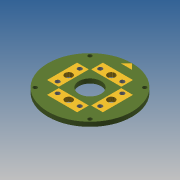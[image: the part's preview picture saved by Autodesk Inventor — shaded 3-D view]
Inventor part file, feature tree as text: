
AUTODESK INVENTOR PART (.ipt)
format: ipt  version: 2014 SP1 (Build 180222100, 222)  size: 210,944 bytes
history: native  units: in
note: dims shown in document units (in); Inventor stores cm internally (conversion verified against a paired STEP export)
features: sketch x11, hole x4, other x4, extrude x3, pattern_circular x3
ambient origin geometry x8: Origin, YZ Plane, XZ Plane, XY Plane, X Axis, Y Axis, Z Axis, Center Point
bodies: Solid1 (feature_tree)
feature tree (25):
  extrude  "Extrusion1"  Depth=0.1in TaperAngle=0.0deg
  extrude  "Extrusion2"  Depth=0.265in
  pattern_circular  "Circular Pattern1"  Count=4 Angle=360.0deg
  hole  "Hole1"  [1 undecoded]
  pattern_circular  "Circular Pattern2"  Count=4 Angle=360.0deg
  hole  "Hole2"  [1 undecoded]
  hole  "Hole3"  [1 undecoded]
  pattern_circular  "Circular Pattern3"  [2 undecoded]
  extrude  "Extrusion3"  TaperAngle=45.0deg  [1 undecoded]
  hole  "Hole4"  [1 undecoded]
  sketch  "Sketch8"  dims[d35=0.115in]
  other  "Pol1_1"
  sketch  "Sketch9"  dims[d36=0.169in d37=0.75in d38=0.375in d39=0.25in d40=0.5635in d41=1.0in d42=0.8108in]
  other  "Pol1_2"
  sketch  "Sketch10"  dims[d43=0.1in d44=0.75in d45=0.375in d46=0.25in d47=0.5635in d48=1.0in d49=0.8108in d50=1.5748in d51=360.0deg]
  other  "Pol2_1"
  sketch  "Sketch11"  dims[d53=0.1in d54=0.0in d55=0.13in d56=0.184in d57=45.0deg d58=0.0in d59=0.0in d60=0.25in d61=0.5in d62=0.5in d63=0.75in d64=0.375in d65=0.25in d66=0.5635in d67=1.0in d68=0.8108in]
  other  "Pol2_2"
  sketch  "Sketch1"  dims[d0=1.9in d1=0.1in d2=0.0in]
  sketch  "Sketch2"  dims[d9=0.68in d10=0.265in]
  sketch  "Sketch3"  dims[d11=0.3663in]
  sketch  "Sketch4"  dims[d12=0.0in d13=0.0in d14=1.5748in d15=360.0deg]
  sketch  "Sketch5"  dims[d22=0.875in d23=45.0deg]
  sketch  "Sketch6"  dims[d24=0.089in]
  sketch  "Sketch7"  dims[d25=0.089in d26=0.75in d27=0.375in d28=0.25in d29=0.5635in d30=1.0in d31=0.8108in d32=1.5748in d33=360.0deg]
note: 7 required parameter values undecoded (feature->parameter linkage not recoverable at this tier; creation-order binding heuristic only, values carry confidence <= 0.55)
